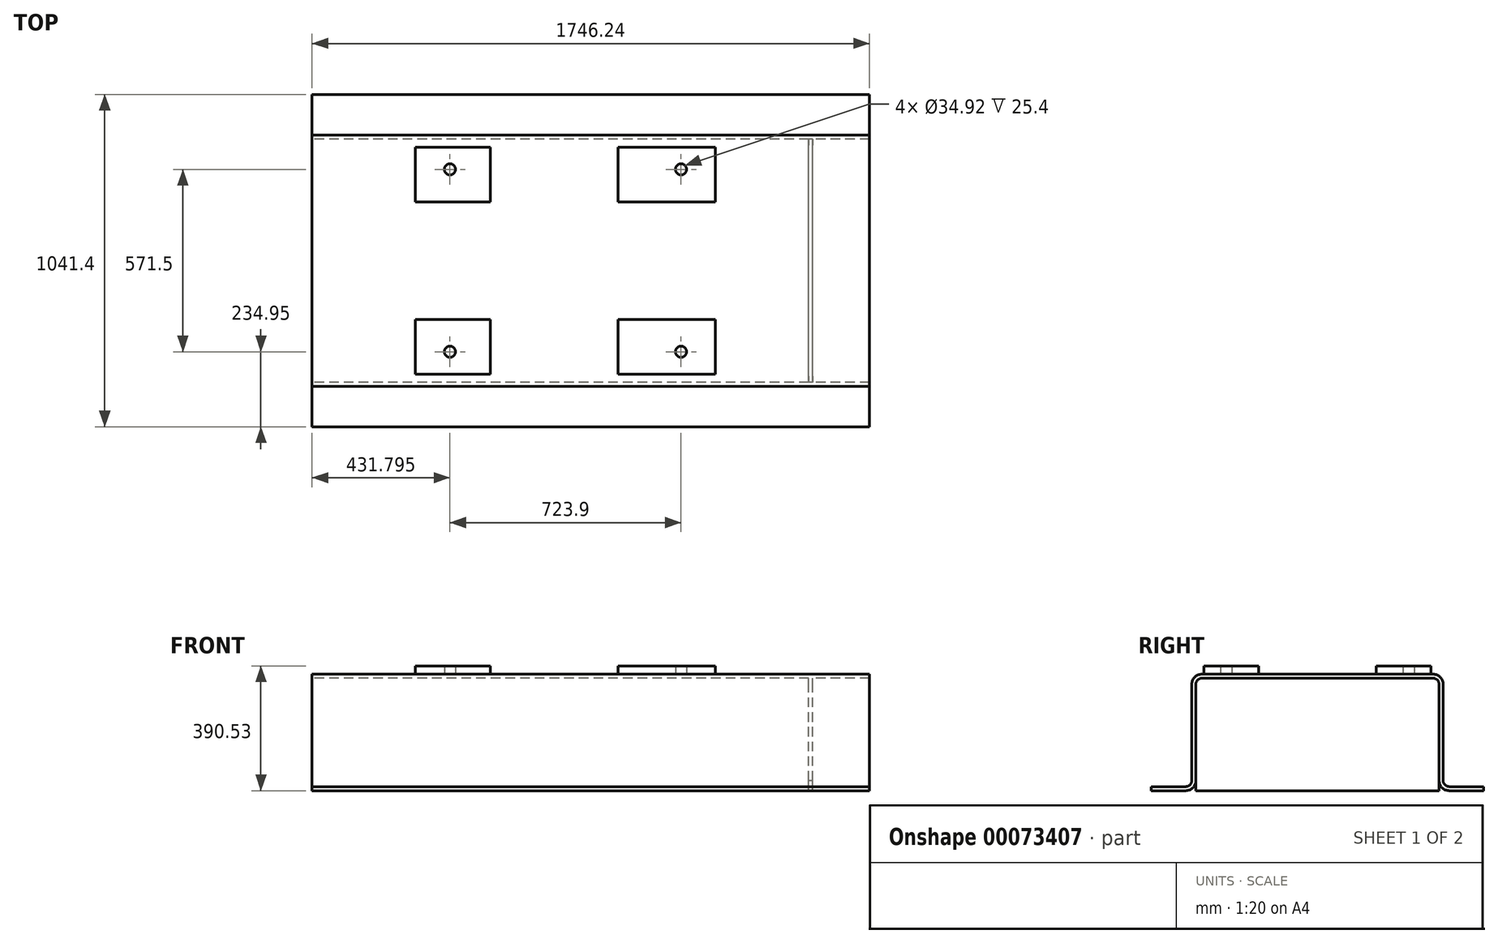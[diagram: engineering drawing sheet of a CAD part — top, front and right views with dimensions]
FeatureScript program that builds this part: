
annotation { "Feature Type Name" : "Feature", "Feature Type Description" : "" }
export const myFeature = defineFeature(function(context is Context, id is Id, definition is map)
    precondition{}
    {
        {
            var Q0;
            Q0=qCreatedBy(makeId("Right.planeOp"),FACE);
            var sketch = newSketch(context, id + "F0", { "sketchPlane" : qUnion([Q0])});
            skLineSegment(sketch, "E0", {"start": v(412.75, 0) * mm, "end": v(520.7, 0) * mm});
            skLineSegment(sketch, "E1.0", {"start": v(0, 365.13) * mm, "end": v(361.95, 365.13) * mm});
            skLineSegment(sketch, "E2", {"start": v(0, -73.94) * mm, "end": v(0, 485.88) * mm, "construction": true});
            skLineSegment(sketch, "E3.0", {"start": v(412.75, 12.7) * mm, "end": v(520.7, 12.7) * mm});
            skLineSegment(sketch, "E4.0", {"start": v(0, 352.43) * mm, "end": v(361.95, 352.43) * mm});
            skLineSegment(sketch, "E5.0", {"start": v(393.7, 31.75) * mm, "end": v(393.7, 333.38) * mm});
            skLineSegment(sketch, "E6.0", {"start": v(381, 31.75) * mm, "end": v(381, 333.38) * mm});
            skArc(sketch, "E7.filletArc", {"start": v(381, 333.38) * mm, "mid": v(375.42, 346.85) * mm, "end": v(361.95, 352.43) * mm});
            skArc(sketch, "E8.filletArc", {"start": v(393.7, 31.75) * mm, "mid": v(399.28, 18.28) * mm, "end": v(412.75, 12.7) * mm});
            skArc(sketch, "E9.filletArc", {"start": v(393.7, 333.38) * mm, "mid": v(384.4, 355.83) * mm, "end": v(361.95, 365.13) * mm});
            skPoint(sketch, "E10.newPointB", {"position": v(-520.7, 0) * mm});
            skArc(sketch, "E10.filletArc", {"start": v(381, 31.75) * mm, "mid": v(390.3, 9.3) * mm, "end": v(412.75, 0) * mm});
            skLineSegment(sketch, "E11", {"start": v(520.7, 12.7) * mm, "end": v(520.7, 0) * mm});
            skLineSegment(sketch, "E12.MirrorCS", {"start": v(-520.7, 12.7) * mm, "end": v(-520.7, 0) * mm});
            skArc(sketch, "E13.MirrorCS", {"start": v(-381, 333.38) * mm, "mid": v(-375.42, 346.85) * mm, "end": v(-361.95, 352.43) * mm});
            skArc(sketch, "E14.MirrorCS", {"start": v(-393.7, 31.75) * mm, "mid": v(-399.28, 18.28) * mm, "end": v(-412.75, 12.7) * mm});
            skArc(sketch, "E15.MirrorCS", {"start": v(-381, 31.75) * mm, "mid": v(-390.3, 9.3) * mm, "end": v(-412.75, 0) * mm});
            skLineSegment(sketch, "E16.MirrorCS", {"start": v(-412.75, 0) * mm, "end": v(-520.7, 0) * mm});
            skLineSegment(sketch, "E17.MirrorCS", {"start": v(0, 365.13) * mm, "end": v(-361.95, 365.13) * mm});
            skLineSegment(sketch, "E18.MirrorCS", {"start": v(-412.75, 12.7) * mm, "end": v(-520.7, 12.7) * mm});
            skLineSegment(sketch, "E19.MirrorCS", {"start": v(-381, 31.75) * mm, "end": v(-381, 333.38) * mm});
            skArc(sketch, "E20.MirrorCS", {"start": v(-393.7, 333.38) * mm, "mid": v(-384.4, 355.83) * mm, "end": v(-361.95, 365.13) * mm});
            skLineSegment(sketch, "E21.MirrorCS", {"start": v(0, 352.43) * mm, "end": v(-361.95, 352.43) * mm});
            skLineSegment(sketch, "E22.MirrorCS", {"start": v(-393.7, 31.75) * mm, "end": v(-393.7, 333.38) * mm});
            skSolve(sketch);
        }
        {
            var Q0;
            Q0 = qSketchRegion(id + "F0", true);
            extrude(context, id + "F1", {"entities" : qUnion([Q0]), "endBound" : BoundingType.SYMMETRIC, "depth" : 1746.25 * mm});
        }
        {
            var Q0;
            Q0=makeQuery(id+"F1.opExtrude","SWEPT_FACE",FACE,{"disambiguationData":[OSD([sQuery(id+"F0.wireOp",EDGE,"E1.0"),sQuery(id+"F0.wireOp",EDGE,"E17.MirrorCS")])]});
            var sketch = newSketch(context, id + "F2", { "sketchPlane" : qUnion([Q0])});
            skLineSegment(sketch, "E23.0", {"start": v(873.12, -361.95) * mm, "end": v(873.12, 361.95) * mm, "construction": true});
            skLineSegment(sketch, "E24.0", {"start": v(644.52, -361.95) * mm, "end": v(644.52, 361.95) * mm, "construction": true});
            skLineSegment(sketch, "E25.0", {"start": v(-79.38, -361.95) * mm, "end": v(-79.38, 361.95) * mm, "construction": true});
            skLineSegment(sketch, "E26.0", {"start": v(390.52, 184.15) * mm, "end": v(390.52, 355.6) * mm});
            skLineSegment(sketch, "E27", {"start": v(-977.5, 0) * mm, "end": v(952.25, 0) * mm, "construction": true});
            skLineSegment(sketch, "E28.0", {"start": v(-549.28, 184.15) * mm, "end": v(-314.33, 184.15) * mm});
            skLineSegment(sketch, "E29.0", {"start": v(-549.28, 355.6) * mm, "end": v(-314.33, 355.6) * mm});
            skLineSegment(sketch, "E30.trimOffspring", {"start": v(-549.28, 184.15) * mm, "end": v(-549.28, 355.6) * mm});
            skLineSegment(sketch, "E31.trimOffspring", {"start": v(85.72, 184.15) * mm, "end": v(390.52, 184.15) * mm});
            skLineSegment(sketch, "E32.trimOffspring", {"start": v(85.72, 355.6) * mm, "end": v(390.52, 355.6) * mm});
            skLineSegment(sketch, "E33.trimOffspring", {"start": v(-314.33, 184.15) * mm, "end": v(-314.33, 355.6) * mm});
            skLineSegment(sketch, "E34.trimOffspring", {"start": v(85.72, 184.15) * mm, "end": v(85.72, 355.6) * mm});
            skLineSegment(sketch, "E35.0", {"start": v(-441.33, -361.95) * mm, "end": v(-441.33, 361.95) * mm, "construction": true});
            skLineSegment(sketch, "E36.0", {"start": v(-977.5, 285.75) * mm, "end": v(952.25, 285.75) * mm, "construction": true});
            skCircle(sketch, "E37", {"center": v(-441.33, 285.75) * mm, "radius": 17.46 * mm});
            skCircle(sketch, "E38.MirrorC", {"center": v(282.57, 285.75) * mm, "radius": 17.46 * mm});
            skLineSegment(sketch, "E39.MirrorCS", {"start": v(85.72, -355.6) * mm, "end": v(390.52, -355.6) * mm});
            skLineSegment(sketch, "E40.MirrorCS", {"start": v(-549.28, -355.6) * mm, "end": v(-314.33, -355.6) * mm});
            skLineSegment(sketch, "E41.MirrorCS", {"start": v(-549.28, -184.15) * mm, "end": v(-549.28, -355.6) * mm});
            skLineSegment(sketch, "E42.MirrorCS", {"start": v(-549.28, -184.15) * mm, "end": v(-314.33, -184.15) * mm});
            skLineSegment(sketch, "E43.MirrorCS", {"start": v(390.52, -184.15) * mm, "end": v(390.52, -355.6) * mm});
            skLineSegment(sketch, "E44.MirrorCS", {"start": v(85.72, -184.15) * mm, "end": v(85.72, -355.6) * mm});
            skCircle(sketch, "E45.MirrorC", {"center": v(282.57, -285.75) * mm, "radius": 17.46 * mm});
            skLineSegment(sketch, "E46.MirrorCS", {"start": v(-314.33, -184.15) * mm, "end": v(-314.33, -355.6) * mm});
            skCircle(sketch, "E47.MirrorC", {"center": v(-441.33, -285.75) * mm, "radius": 17.46 * mm});
            skLineSegment(sketch, "E48.MirrorCS", {"start": v(85.72, -184.15) * mm, "end": v(390.52, -184.15) * mm});
            skSolve(sketch);
        }
        {
            var Q0;
            Q0 = qSketchRegion(id + "F2", true);
            extrude(context, id + "F3", {"entities" : qUnion([Q0]), "operationType" : NewBodyOperationType.ADD, "depth" : 25.4 * mm});
        }
        {
            var Q0;
            Q0=makeQuery(id+"F1.opExtrude","SWEPT_FACE",FACE,{"disambiguationData":[OSD([sQuery(id+"F0.wireOp",EDGE,"E4.0"),sQuery(id+"F0.wireOp",EDGE,"E21.MirrorCS")])]});
            var sketch = newSketch(context, id + "F4", { "sketchPlane" : qUnion([Q0])});
            skLineSegment(sketch, "E49.0", {"start": v(873.12, -361.95) * mm, "end": v(873.12, 361.95) * mm, "construction": true});
            skLineSegment(sketch, "E50.0", {"start": v(695.32, -381) * mm, "end": v(695.32, 381) * mm, "construction": true});
            skLineSegment(sketch, "E51.0.1", {"start": v(-873.12, 381) * mm, "end": v(873.12, 381) * mm});
            skLineSegment(sketch, "E51.0.3", {"start": v(873.12, 381) * mm, "end": v(-873.12, 381) * mm});
            skLineSegment(sketch, "E52.0.1", {"start": v(-873.12, -381) * mm, "end": v(873.12, -381) * mm});
            skLineSegment(sketch, "E52.0.3", {"start": v(873.12, -381) * mm, "end": v(-873.12, -381) * mm});
            skLineSegment(sketch, "E53.bottom", {"start": v(695.32, 381) * mm, "end": v(682.62, 381) * mm});
            skLineSegment(sketch, "E53.top", {"start": v(695.32, -381) * mm, "end": v(682.62, -381) * mm});
            skLineSegment(sketch, "E53.left", {"start": v(695.32, 381) * mm, "end": v(695.32, -381) * mm});
            skLineSegment(sketch, "E53.right", {"start": v(682.62, 381) * mm, "end": v(682.62, -381) * mm});
            skSolve(sketch);
        }
        {
            var Q0;
            Q0 = qSketchRegion(id + "F4", true);
            var Q1;
            Q1=makeQuery(id+"F1.opExtrude","SWEPT_FACE",FACE,{"disambiguationData":[OSD([sQuery(id+"F0.wireOp",EDGE,"E16.MirrorCS")])]});
            extrude(context, id + "F5", {"entities" : qUnion([Q0]), "operationType" : NewBodyOperationType.ADD, "endBound" : BoundingType.UP_TO_SURFACE, "endBoundEntityFace" : qUnion([Q1]), "depth" : 25.4 * mm});
        }
    });
